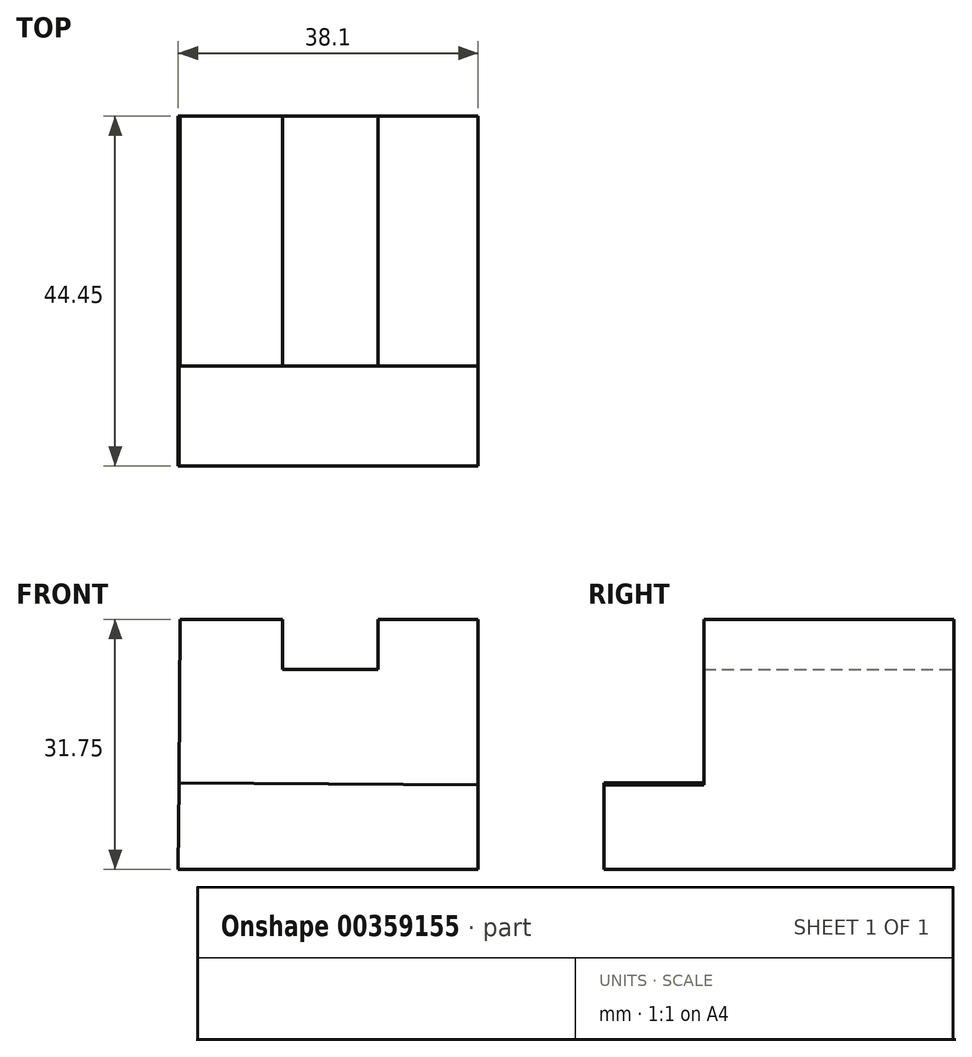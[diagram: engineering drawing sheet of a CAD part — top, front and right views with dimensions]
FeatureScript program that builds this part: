
annotation { "Feature Type Name" : "Feature", "Feature Type Description" : "" }
export const myFeature = defineFeature(function(context is Context, id is Id, definition is map)
    precondition{}
    {
        {
            var Q0;
            Q0=qCreatedBy(makeId("Front.planeOp"),FACE);
            var sketch = newSketch(context, id + "F0", { "sketchPlane" : qUnion([Q0])});
            skLineSegment(sketch, "E0", {"start": v(2.8, 0) * mm, "end": v(40.9, 0) * mm});
            skLineSegment(sketch, "E1", {"start": v(40.9, 0) * mm, "end": v(40.9, 31.75) * mm});
            skLineSegment(sketch, "E2", {"start": v(40.9, 31.75) * mm, "end": v(28.2, 31.75) * mm});
            skLineSegment(sketch, "E3", {"start": v(28.2, 31.75) * mm, "end": v(28.2, 25.4) * mm});
            skLineSegment(sketch, "E4", {"start": v(28.2, 25.4) * mm, "end": v(16.05, 25.4) * mm});
            skLineSegment(sketch, "E5", {"start": v(16.05, 25.4) * mm, "end": v(16.05, 31.75) * mm});
            skLineSegment(sketch, "E6", {"start": v(16.05, 31.75) * mm, "end": v(3.04, 31.75) * mm});
            skLineSegment(sketch, "E7", {"start": v(3.04, 31.75) * mm, "end": v(2.8, 0) * mm});
            skLineSegment(sketch, "E8", {"start": v(3, 25.12) * mm, "end": v(16.05, 25.4) * mm});
            skLineSegment(sketch, "E9", {"start": v(28.2, 25.4) * mm, "end": v(40.9, 25.3) * mm});
            skLineSegment(sketch, "E10", {"start": v(3, 25.12) * mm, "end": v(2.83, 3.59) * mm});
            skLineSegment(sketch, "E11", {"start": v(2.83, 3.59) * mm, "end": v(40.9, 3.3) * mm});
            skLineSegment(sketch, "E12", {"start": v(40.9, 25.3) * mm, "end": v(40.9, 3.3) * mm});
            skSolve(sketch);
        }
        {
            var Q0;
            Q0 = qSketchRegion(id + "F0", true);
            extrude(context, id + "F1", {"entities" : qUnion([Q0]), "depth" : 19.05 * mm});
        }
        {
            var Q0;
            Q0 = qSketchRegion(id + "F0", true);
            extrude(context, id + "F2", {"entities" : qUnion([Q0]), "operationType" : NewBodyOperationType.REMOVE, "oppositeDirection" : true, "depth" : 25.4 * mm});
        }
        {
            var Q0;
            Q0=makeQuery(id+"F1.opExtrude","CAP_FACE",FACE,{"disambiguationData":[OSD([sQuery(id+"F0.wireOp",EDGE,"E0"),sQuery(id+"F0.wireOp",EDGE,"E1"),sQuery(id+"F0.wireOp",EDGE,"E2"),sQuery(id+"F0.wireOp",EDGE,"E3"),sQuery(id+"F0.wireOp",EDGE,"E4"),sQuery(id+"F0.wireOp",EDGE,"E5"),sQuery(id+"F0.wireOp",EDGE,"E6"),sQuery(id+"F0.wireOp",EDGE,"E7"),sQuery(id+"F0.wireOp",EDGE,"E10"),sQuery(id+"F0.wireOp",EDGE,"E12")])],"isStart":false});
            extrude(context, id + "F3", {"entities" : qUnion([Q0]), "operationType" : NewBodyOperationType.ADD, "depth" : 25.4 * mm});
        }
        {
            var Q0;
            Q0=makeQuery(id+"F3.opExtrude","CAP_FACE",FACE,{"disambiguationData":[OSD([sQuery(id+"F0.wireOp",EDGE,"E0"),sQuery(id+"F0.wireOp",EDGE,"E1"),sQuery(id+"F0.wireOp",EDGE,"E2"),sQuery(id+"F0.wireOp",EDGE,"E3"),sQuery(id+"F0.wireOp",EDGE,"E4"),sQuery(id+"F0.wireOp",EDGE,"E5"),sQuery(id+"F0.wireOp",EDGE,"E6"),sQuery(id+"F0.wireOp",EDGE,"E7"),sQuery(id+"F0.wireOp",EDGE,"E10"),sQuery(id+"F0.wireOp",EDGE,"E12")])],"isStart":false});
            var sketch = newSketch(context, id + "F4", { "sketchPlane" : qUnion([Q0])});
            skLineSegment(sketch, "E13", {"start": v(2.89, 11) * mm, "end": v(40.9, 10.7) * mm});
            skSolve(sketch);
        }
        {
            var Q0;
            Q0 = qSketchRegion(id + "F4", true);
            var Q1;
            {var subQ1=sQuery(id+"F4.wireOp",EDGE,"E13");Q1=makeQuery(id+"F4.imprint","IMPRINT",FACE,{"disambiguationData":[TD([[makeQuery(id+"F4.imprint","IMPRINT",EDGE,{"derivedFrom":subQ1}),1.0]])]});}
            extrude(context, id + "F5", {"entities" : qUnion([Q0, Q1]), "operationType" : NewBodyOperationType.REMOVE, "oppositeDirection" : true, "depth" : 12.7 * mm});
        }
    });
